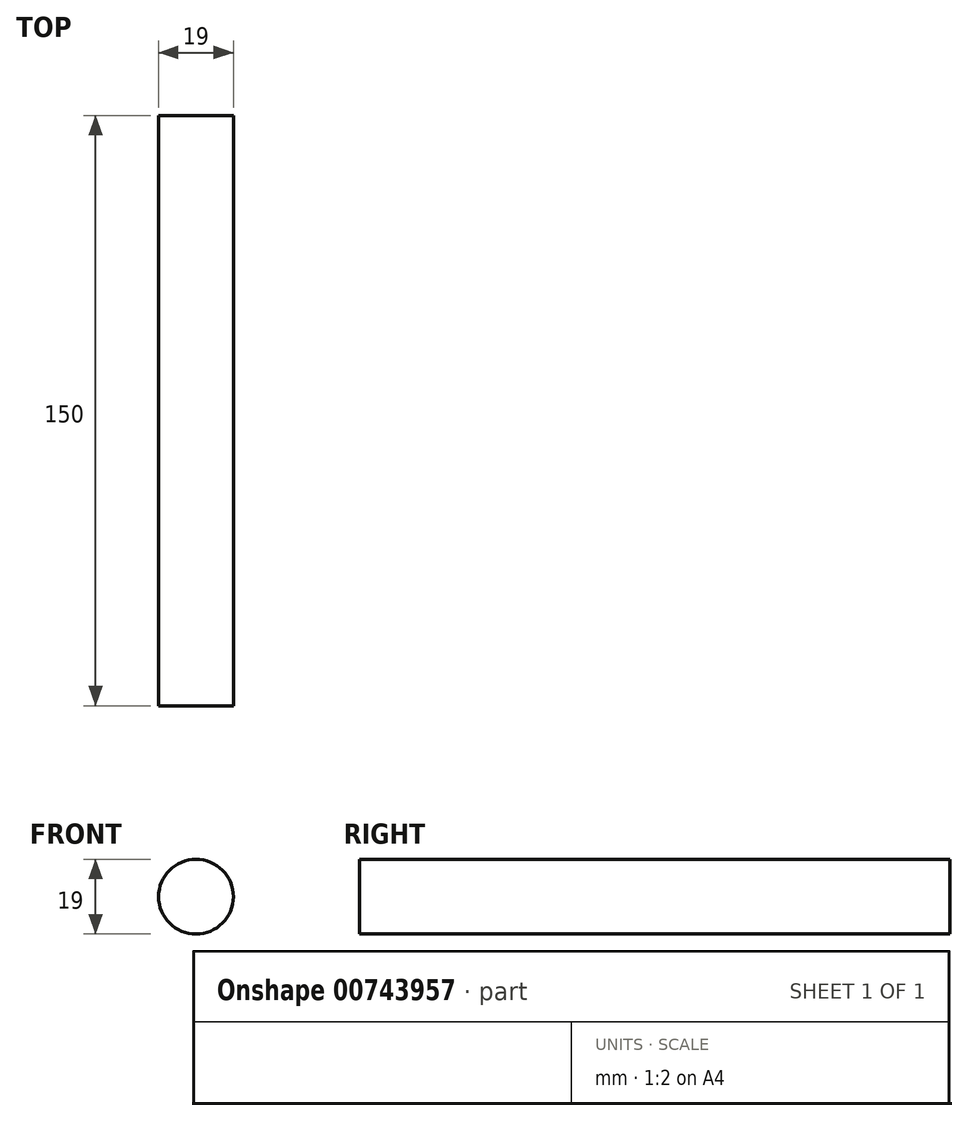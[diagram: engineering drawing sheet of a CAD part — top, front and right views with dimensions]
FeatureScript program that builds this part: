
annotation { "Feature Type Name" : "Feature", "Feature Type Description" : "" }
export const myFeature = defineFeature(function(context is Context, id is Id, definition is map)
    precondition{}
    {
        {
            var Q0;
            Q0=qCreatedBy(makeId("Front.planeOp"),FACE);
            var sketch = newSketch(context, id + "F0", { "sketchPlane" : qUnion([Q0])});
            skCircle(sketch, "E0", {"center": v(1.04, 0) * mm, "radius": 9.5 * mm});
            skSolve(sketch);
        }
        {
            var Q0;
            Q0=makeQuery(id+"F0.imprint","IMPRINT",FACE,{"disambiguationData":[TD([[makeQuery(id+"F0.imprint","IMPRINT",EDGE,{"derivedFrom":sQuery(id+"F0.wireOp",EDGE,"E0")}),1.0]])]});
            extrude(context, id + "F1", {"entities" : qUnion([Q0]), "depth" : 150 * mm, "offsetDistance" : 25 * mm});
        }
    });
